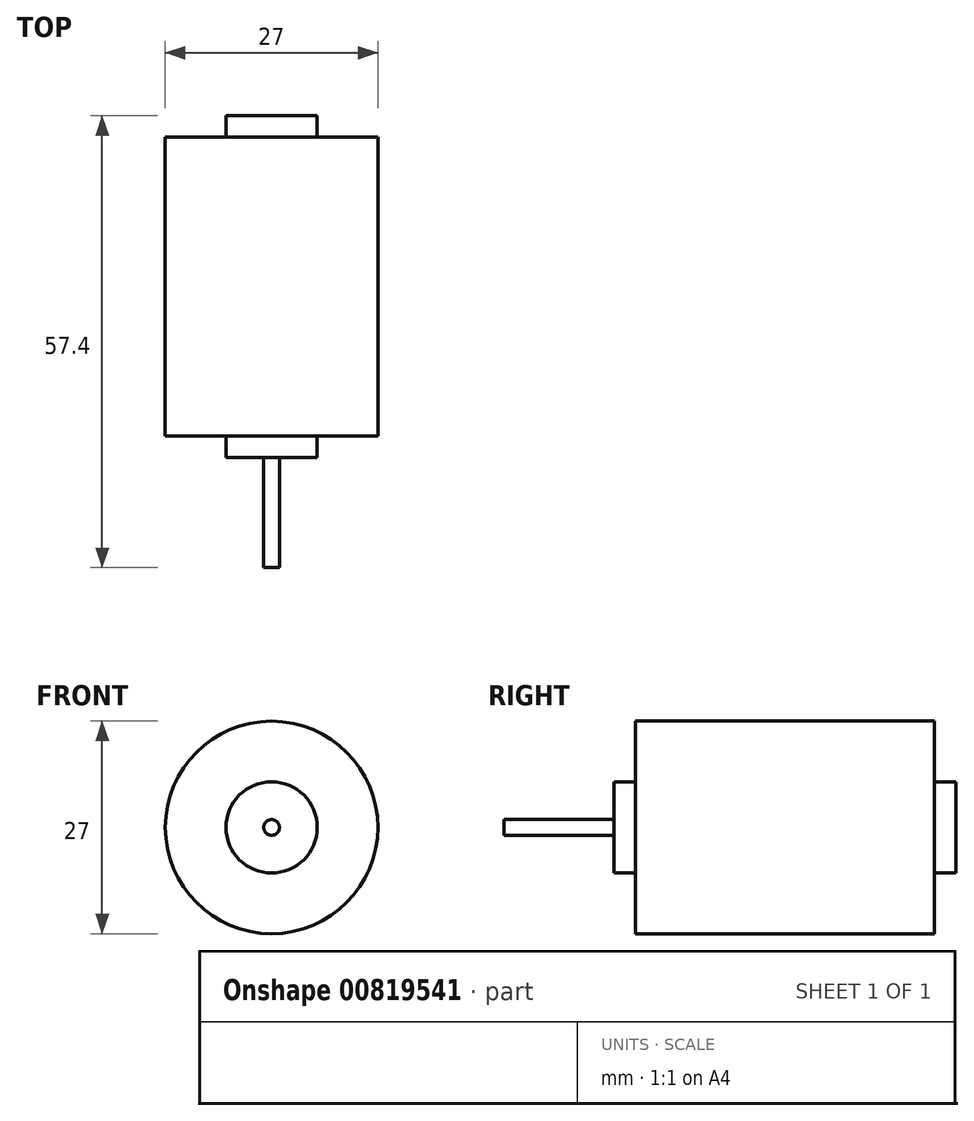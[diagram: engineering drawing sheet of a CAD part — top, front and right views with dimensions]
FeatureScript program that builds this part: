
annotation { "Feature Type Name" : "Feature", "Feature Type Description" : "" }
export const myFeature = defineFeature(function(context is Context, id is Id, definition is map)
    precondition{}
    {
        {
            var Q0;
            Q0=qCreatedBy(makeId("Right.planeOp"),FACE);
            var sketch = newSketch(context, id + "F0", { "sketchPlane" : qUnion([Q0])});
            skLineSegment(sketch, "E0", {"start": v(0, 0) * mm, "end": v(0, -4.8) * mm});
            skLineSegment(sketch, "E1", {"start": v(0, -4.8) * mm, "end": v(-2.7, -4.8) * mm});
            skLineSegment(sketch, "E2", {"start": v(-2.7, -4.8) * mm, "end": v(-2.7, -12.5) * mm});
            skLineSegment(sketch, "E3", {"start": v(-2.7, -12.5) * mm, "end": v(-40.7, -12.5) * mm});
            skLineSegment(sketch, "E4", {"start": v(-40.7, -12.5) * mm, "end": v(-40.7, -4.8) * mm});
            skLineSegment(sketch, "E5", {"start": v(-40.7, -4.8) * mm, "end": v(-43.4, -4.8) * mm});
            skLineSegment(sketch, "E6", {"start": v(-43.4, -4.8) * mm, "end": v(-43.4, 0) * mm});
            skLineSegment(sketch, "E7", {"start": v(-43.4, 0) * mm, "end": v(-57.4, 0) * mm});
            skLineSegment(sketch, "E8", {"start": v(-57.4, 0) * mm, "end": v(-57.4, 1) * mm});
            skLineSegment(sketch, "E9", {"start": v(-57.4, 1) * mm, "end": v(0, 1) * mm});
            skLineSegment(sketch, "E10", {"start": v(0, 1) * mm, "end": v(0, 0) * mm});
            skSolve(sketch);
        }
        {
            var Q0;
            Q0=makeQuery(id+"F0.imprint","IMPRINT",FACE,{"disambiguationData":[TD([[makeQuery(id+"F0.imprint","IMPRINT",EDGE,{"derivedFrom":sQuery(id+"F0.wireOp",EDGE,"E0")}),-1.0]])]});
            var Q1;
            Q1=sQuery(id+"F0.wireOp",EDGE,"E9");
            revolve(context, id + "F1", {"surfaceOperationType" : NewSurfaceOperationType.NEW, "entities" : qUnion([Q0]), "axis" : qUnion([Q1]), "revolveType" : RevolveType.FULL});
        }
    });
